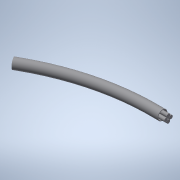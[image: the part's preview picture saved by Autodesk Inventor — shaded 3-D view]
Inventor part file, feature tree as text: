
AUTODESK INVENTOR PART (.ipt)
format: ipt  version: 2020 (Build 240168000, 168)  size: 197,120 bytes
history: native  units: in
note: dims shown in document units (in); Inventor stores cm internally (conversion verified against a paired STEP export)
features: sketch x2, extrude x2, sweep x1
ambient origin geometry x8: Origin, YZ Plane, XZ Plane, XY Plane, X Axis, Y Axis, Z Axis, Center Point
bodies: Solid1 (feature_tree)
feature tree (5):
  sketch  "Sketch2-<F>"  dims[d0=1.875in d1=0.082in]
  sweep  "Sweep1"
  extrude  "Extrusion1"  TaperAngle=0.0deg  [1 undecoded]
  extrude  "Extrusion2"  Depth=0.075in
  sketch  "Sketch1-<F>"  dims[d2=0.005in d7=0.0in d8=0.0in d9=0.0422in d10=1.5748in d12=360.0deg d14=0.075in d15=0.0in d16=0.125in d17=0.0in d18=30.0deg]
note: 1 required parameter value undecoded (feature->parameter linkage not recoverable at this tier; creation-order binding heuristic only, values carry confidence <= 0.55)
